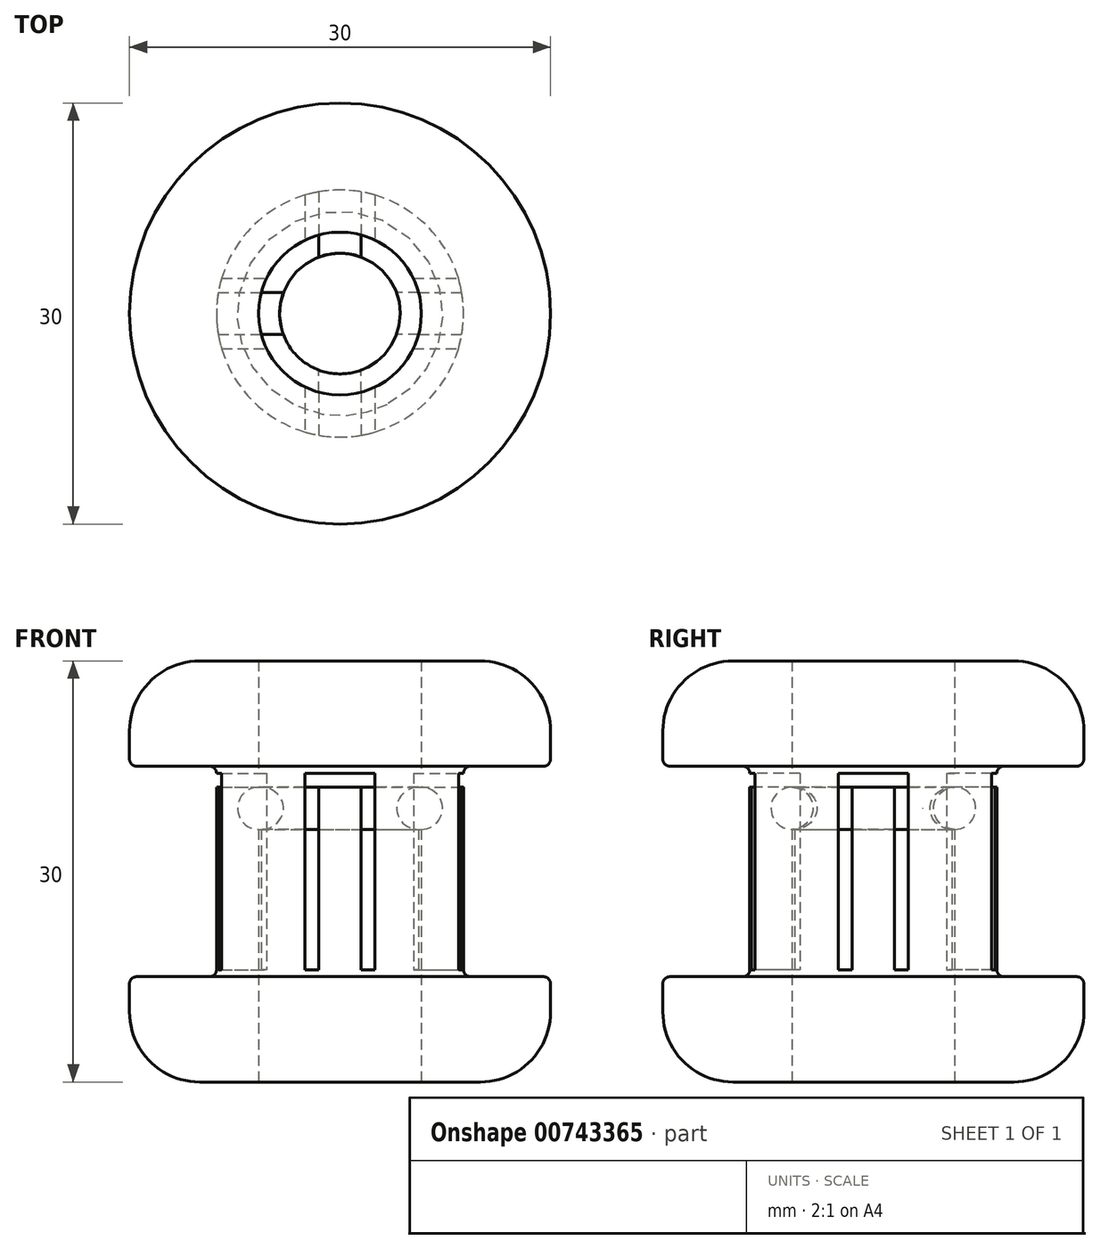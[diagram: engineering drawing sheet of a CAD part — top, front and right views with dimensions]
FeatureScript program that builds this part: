
annotation { "Feature Type Name" : "Feature", "Feature Type Description" : "" }
export const myFeature = defineFeature(function(context is Context, id is Id, definition is map)
    precondition{}
    {
        {
            var Q0;
            Q0=qCreatedBy(makeId("Front.planeOp"),FACE);
            var sketch = newSketch(context, id + "F0", { "sketchPlane" : qUnion([Q0])});
            skLineSegment(sketch, "E0", {"start": v(0, 0) * mm, "end": v(0, 29.89) * mm, "construction": true});
            skLineSegment(sketch, "E1", {"start": v(5.8, 30) * mm, "end": v(5.8, 21) * mm});
            skLineSegment(sketch, "E2", {"start": v(15, 23) * mm, "end": v(15, 25) * mm});
            skLineSegment(sketch, "E3", {"start": v(5.8, 0) * mm, "end": v(10, 0) * mm});
            skLineSegment(sketch, "E4", {"start": v(5.8, 30) * mm, "end": v(10, 30) * mm});
            skLineSegment(sketch, "E5", {"start": v(8.8, 22) * mm, "end": v(8.8, 8) * mm});
            skLineSegment(sketch, "E6", {"start": v(9.3, 7.5) * mm, "end": v(14.5, 7.5) * mm});
            skLineSegment(sketch, "E7", {"start": v(9.3, 22.5) * mm, "end": v(14.5, 22.5) * mm});
            skPoint(sketch, "E8.visualSharp", {"position": v(15, 30) * mm});
            skArc(sketch, "E8.filletArc", {"start": v(15, 25) * mm, "mid": v(13.54, 28.54) * mm, "end": v(10, 30) * mm});
            skPoint(sketch, "E9.visualSharp", {"position": v(15, 0) * mm});
            skArc(sketch, "E9.filletArc", {"start": v(10, 0) * mm, "mid": v(13.54, 1.46) * mm, "end": v(15, 5) * mm});
            skArc(sketch, "E10", {"start": v(5.8, 21) * mm, "mid": v(4.3, 19.5) * mm, "end": v(5.8, 18) * mm});
            skLineSegment(sketch, "E11.trimOffspring", {"start": v(5.8, 18) * mm, "end": v(5.8, 0) * mm});
            skPoint(sketch, "E12.visualSharp", {"position": v(8.8, 22.5) * mm});
            skArc(sketch, "E12.filletArc", {"start": v(9.3, 22.5) * mm, "mid": v(8.95, 22.35) * mm, "end": v(8.8, 22) * mm});
            skPoint(sketch, "E13.visualSharp", {"position": v(8.8, 7.5) * mm});
            skArc(sketch, "E13.filletArc", {"start": v(8.8, 8) * mm, "mid": v(8.95, 7.65) * mm, "end": v(9.3, 7.5) * mm});
            skArc(sketch, "E14.filletArc", {"start": v(14.5, 22.5) * mm, "mid": v(14.85, 22.65) * mm, "end": v(15, 23) * mm});
            skLineSegment(sketch, "E15", {"start": v(15, 5) * mm, "end": v(15, 7) * mm});
            skPoint(sketch, "E16.visualSharp", {"position": v(15, 7.5) * mm});
            skArc(sketch, "E16.filletArc", {"start": v(15, 7) * mm, "mid": v(14.85, 7.35) * mm, "end": v(14.5, 7.5) * mm});
            skSolve(sketch);
        }
        {
            var Q0;
            Q0 = qSketchRegion(id + "F0", true);
            var Q1;
            Q1=sQuery(id+"F0.wireOp",EDGE,"E0");
            revolve(context, id + "F1", {"surfaceOperationType" : NewSurfaceOperationType.NEW, "entities" : qUnion([Q0]), "axis" : qUnion([Q1]), "revolveType" : RevolveType.FULL});
        }
        {
            var Q0;
            Q0=qCreatedBy(makeId("Right.planeOp"),FACE);
            var sketch = newSketch(context, id + "F2", { "sketchPlane" : qUnion([Q0])});
            skLineSegment(sketch, "E17", {"start": v(-1.5, 8) * mm, "end": v(-1.5, 21) * mm});
            skLineSegment(sketch, "E18", {"start": v(-2.5, 8) * mm, "end": v(-2.5, 22) * mm});
            skLineSegment(sketch, "E19", {"start": v(1.5, 8) * mm, "end": v(1.5, 21) * mm});
            skLineSegment(sketch, "E20", {"start": v(2.5, 8) * mm, "end": v(2.5, 22) * mm});
            skLineSegment(sketch, "E21", {"start": v(-1.5, 21) * mm, "end": v(1.5, 21) * mm});
            skLineSegment(sketch, "E22", {"start": v(-2.5, 22) * mm, "end": v(2.5, 22) * mm});
            skPoint(sketch, "E23.orphan", {"position": v(16.3, 21) * mm});
            skLineSegment(sketch, "E24.0", {"start": v(2.5, 8) * mm, "end": v(1.5, 8) * mm});
            skPoint(sketch, "E25.orphan", {"position": v(-8.8, 8) * mm});
            skPoint(sketch, "E26.orphan", {"position": v(8.8, 8) * mm});
            skLineSegment(sketch, "E27.trimOffspring", {"start": v(-1.5, 8) * mm, "end": v(-2.5, 8) * mm});
            skSolve(sketch);
        }
        {
            var Q0;
            Q0 = qSketchRegion(id + "F2", true);
            extrude(context, id + "F3", {"entities" : qUnion([Q0]), "operationType" : NewBodyOperationType.REMOVE, "oppositeDirection" : true, "depth" : 25 * mm, "offsetDistance" : 25 * mm, "hasSecondDirection" : true, "secondDirectionOppositeDirection" : false, "secondDirectionDepth" : 25 * mm});
        }
        {
            var Q0;
            Q0=qCreatedBy(makeId("Front.planeOp"),FACE);
            var sketch = newSketch(context, id + "F4", { "sketchPlane" : qUnion([Q0])});
            skLineSegment(sketch, "E28", {"start": v(1.5, 8) * mm, "end": v(1.5, 21) * mm});
            skLineSegment(sketch, "E29", {"start": v(2.5, 8) * mm, "end": v(2.5, 22) * mm});
            skLineSegment(sketch, "E30", {"start": v(-1.5, 8) * mm, "end": v(-1.5, 21) * mm});
            skLineSegment(sketch, "E31", {"start": v(-2.5, 8) * mm, "end": v(-2.5, 22) * mm});
            skLineSegment(sketch, "E32", {"start": v(2.5, 22) * mm, "end": v(-2.5, 22) * mm});
            skLineSegment(sketch, "E33", {"start": v(2.54, 21) * mm, "end": v(2.5, 21) * mm});
            skLineSegment(sketch, "E34.0", {"start": v(-2.5, 8) * mm, "end": v(-1.5, 8) * mm});
            skLineSegment(sketch, "E35.trimOffspring", {"start": v(1.5, 21) * mm, "end": v(-1.5, 21) * mm});
            skPoint(sketch, "E36.orphan", {"position": v(-8.44, 8) * mm});
            skLineSegment(sketch, "E37.trimOffspring", {"start": v(1.5, 8) * mm, "end": v(2.5, 8) * mm});
            skPoint(sketch, "E38.orphan", {"position": v(8.44, 8) * mm});
            skSolve(sketch);
        }
        {
            var Q0;
            Q0 = qSketchRegion(id + "F4", true);
            extrude(context, id + "F5", {"entities" : qUnion([Q0]), "operationType" : NewBodyOperationType.REMOVE, "oppositeDirection" : true, "depth" : 25 * mm, "offsetDistance" : 25 * mm, "hasSecondDirection" : true, "secondDirectionOppositeDirection" : false, "secondDirectionDepth" : 25 * mm});
        }
        {
            var Q0;
            Q0=makeQuery(id+"F1.opRevolve","SWEPT_FACE",FACE,{"disambiguationData":[OSD([sQuery(id+"F0.wireOp",EDGE,"E4")])]});
            var sketch = newSketch(context, id + "F6", { "sketchPlane" : qUnion([Q0])});
            skArc(sketch, "E39.0", {"start": v(-2.5, 5.23) * mm, "mid": v(-4.1, 4.1) * mm, "end": v(-5.23, 2.5) * mm});
            skFitSpline(sketch, "E40.0", {"points": [v(-5.23, 2.5) * mm, v(-4.66, 2.5) * mm, v(-4.08, 2.5) * mm, v(-3.5, 2.5) * mm]});
            skFitSpline(sketch, "E41.0", {"points": [v(-2.5, 5.23) * mm, v(-2.5, 4.66) * mm, v(-2.5, 4.08) * mm, v(-2.5, 3.5) * mm]});
            skLineSegment(sketch, "E42", {"start": v(-3.5, 2.5) * mm, "end": v(-2.5, 3.5) * mm});
            skArc(sketch, "E43.1.0", {"start": v(-5.23, -2.5) * mm, "mid": v(-4.1, -4.1) * mm, "end": v(-2.5, -5.23) * mm});
            skArc(sketch, "E43.2.0", {"start": v(2.5, -5.23) * mm, "mid": v(4.1, -4.1) * mm, "end": v(5.23, -2.5) * mm});
            skArc(sketch, "E44.3.3.0", {"start": v(5.23, 2.5) * mm, "mid": v(4.1, 4.1) * mm, "end": v(2.5, 5.23) * mm});
            skFitSpline(sketch, "E45.0", {"points": [v(2.5, 5.23) * mm, v(2.5, 4.66) * mm, v(2.5, 4.08) * mm, v(2.5, 3.5) * mm]});
            skFitSpline(sketch, "E46.0", {"points": [v(5.23, 2.5) * mm, v(4.66, 2.5) * mm, v(4.08, 2.5) * mm, v(3.5, 2.5) * mm]});
            skFitSpline(sketch, "E47.0", {"points": [v(5.23, -2.5) * mm, v(4.66, -2.5) * mm, v(4.08, -2.5) * mm, v(3.5, -2.5) * mm]});
            skFitSpline(sketch, "E48.0", {"points": [v(2.5, -5.23) * mm, v(2.5, -4.66) * mm, v(2.5, -4.08) * mm, v(2.5, -3.5) * mm]});
            skFitSpline(sketch, "E49.0", {"points": [v(-2.5, -5.23) * mm, v(-2.5, -4.66) * mm, v(-2.5, -4.08) * mm, v(-2.5, -3.5) * mm]});
            skFitSpline(sketch, "E50.0", {"points": [v(-5.23, -2.5) * mm, v(-4.66, -2.5) * mm, v(-4.08, -2.5) * mm, v(-3.5, -2.5) * mm]});
            skLineSegment(sketch, "E51", {"start": v(2.5, 3.5) * mm, "end": v(3.5, 2.5) * mm});
            skLineSegment(sketch, "E52", {"start": v(3.5, -2.5) * mm, "end": v(2.5, -3.5) * mm});
            skLineSegment(sketch, "E53", {"start": v(-3.5, -2.5) * mm, "end": v(-2.5, -3.5) * mm});
            skSolve(sketch);
        }
        {
            var Q0;
            Q0 = qSketchRegion(id + "F6", true);
            extrude(context, id + "F7", {"entities" : qUnion([Q0]), "operationType" : NewBodyOperationType.REMOVE, "endBound" : BoundingType.THROUGH_ALL, "oppositeDirection" : true, "depth" : 25 * mm, "offsetDistance" : 25 * mm});
        }
    });
